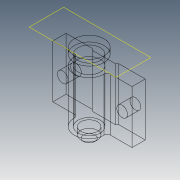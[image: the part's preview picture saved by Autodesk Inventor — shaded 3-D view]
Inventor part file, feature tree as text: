
AUTODESK INVENTOR PART (.ipt)
format: ipt  version: 2018.3 (Build 223284000, 284)  size: 146,944 bytes
history: native  units: in
note: dims shown in document units (in); Inventor stores cm internally (conversion verified against a paired STEP export)
features: plane x1, fillet x1, other x1
ambient origin geometry x8: Origin, YZ Plane, XZ Plane, XY Plane, X Axis, Y Axis, Z Axis, Center Point
bodies: Solid1 (feature_tree), Solid2 (feature_tree)
feature tree (3):
  plane  "Work Plane1"
  fillet  "Fillet2"  Radius=0.375in
  other  "Round Face"
